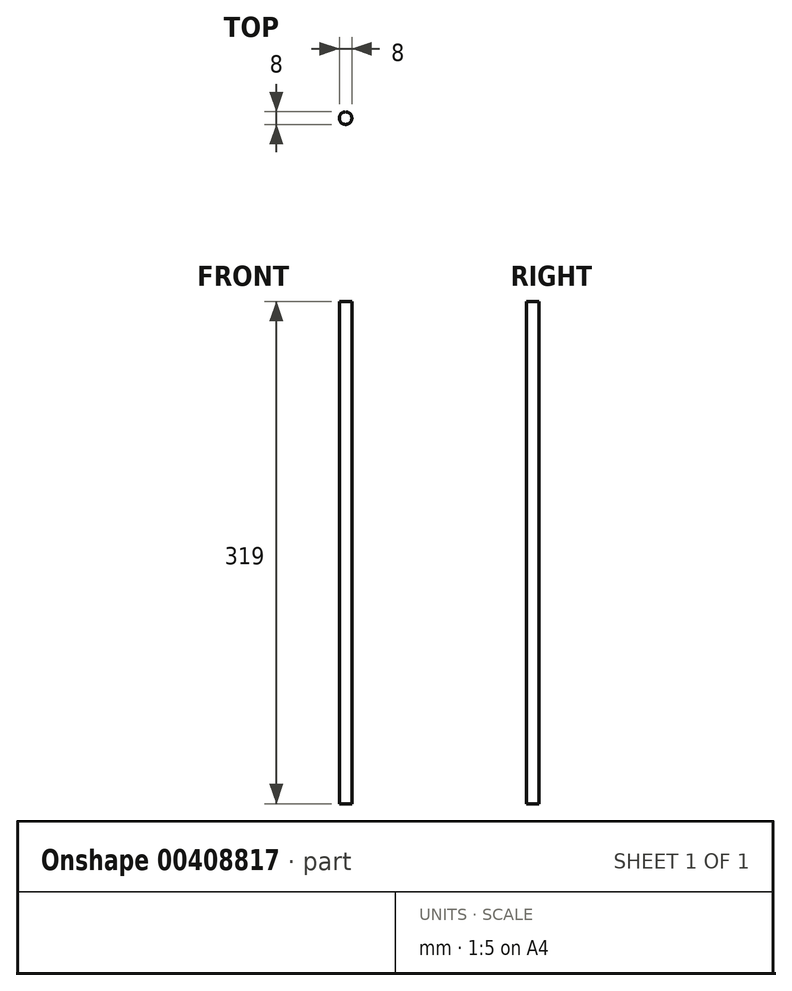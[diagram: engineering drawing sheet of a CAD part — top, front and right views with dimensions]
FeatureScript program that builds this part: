
annotation { "Feature Type Name" : "Feature", "Feature Type Description" : "" }
export const myFeature = defineFeature(function(context is Context, id is Id, definition is map)
    precondition{}
    {
        {
            var Q0;
            Q0=qCreatedBy(makeId("Top.planeOp"),FACE);
            var sketch = newSketch(context, id + "F0", { "sketchPlane" : qUnion([Q0])});
            skCircle(sketch, "E0", {"center": v(0, 0) * mm, "radius": 4 * mm});
            skSolve(sketch);
        }
        {
            var Q0;
            Q0=makeQuery(id+"F0.imprint","IMPRINT",FACE,{"disambiguationData":[TD([[makeQuery(id+"F0.imprint","IMPRINT",EDGE,{"derivedFrom":sQuery(id+"F0.wireOp",EDGE,"E0")}),1.0]])]});
            var Q1;
            Q1=sQuery(id+"F0.wireOp",EDGE,"E0");
            extrude(context, id + "F1", {"entities" : qUnion([Q0]), "surfaceEntities" : qUnion([Q1]), "depth" : 319 * mm});
        }
    });
